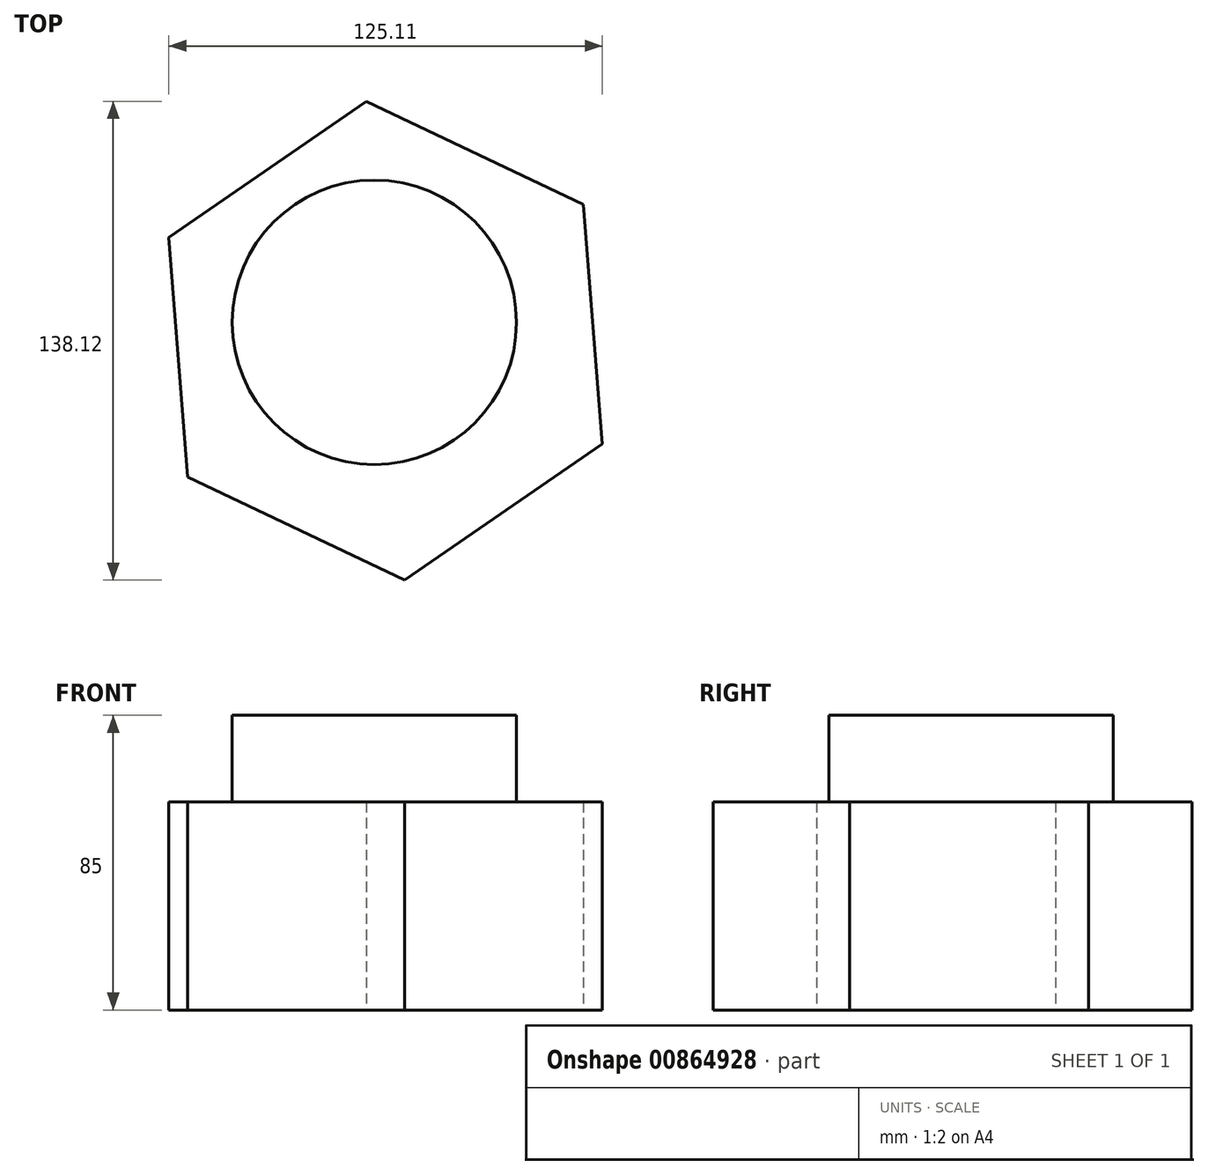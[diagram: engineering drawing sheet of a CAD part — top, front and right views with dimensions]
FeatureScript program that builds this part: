
annotation { "Feature Type Name" : "Feature", "Feature Type Description" : "" }
export const myFeature = defineFeature(function(context is Context, id is Id, definition is map)
    precondition{}
    {
        {
            var Q0;
            Q0=qCreatedBy(makeId("Top.planeOp"),FACE);
            var sketch = newSketch(context, id + "F0", { "sketchPlane" : qUnion([Q0])});
            skCircle(sketch, "E0.cCircle", {"center": v(116.54, 148.1) * mm, "radius": 60 * mm, "construction": true});
            skLineSegment(sketch, "E0.0", {"start": v(53.99, 177.88) * mm, "end": v(111.05, 217.17) * mm});
            skLineSegment(sketch, "E0.1", {"start": v(111.05, 217.17) * mm, "end": v(173.6, 187.4) * mm});
            skLineSegment(sketch, "E0.2", {"start": v(173.6, 187.4) * mm, "end": v(179.1, 118.33) * mm});
            skLineSegment(sketch, "E0.3", {"start": v(179.1, 118.33) * mm, "end": v(122.04, 79.05) * mm});
            skLineSegment(sketch, "E0.4", {"start": v(122.04, 79.05) * mm, "end": v(59.48, 108.82) * mm});
            skLineSegment(sketch, "E0.5", {"start": v(59.48, 108.82) * mm, "end": v(53.99, 177.88) * mm});
            skPoint(sketch, "E0.0.midPoint", {"position": v(82.52, 197.53) * mm});
            skSolve(sketch);
        }
        {
            var Q0;
            Q0=makeQuery(id+"F0.imprint","IMPRINT",FACE,{"disambiguationData":[TD([[makeQuery(id+"F0.imprint","IMPRINT",EDGE,{"derivedFrom":sQuery(id+"F0.wireOp",EDGE,"E0.0")}),-1.0]])]});
            extrude(context, id + "F1", {"entities" : qUnion([Q0]), "depth" : 60 * mm, "offsetDistance" : 25 * mm});
        }
        {
            var Q0;
            Q0=makeQuery(id+"F1.opExtrude","CAP_FACE",FACE,{"disambiguationData":[OSD([sQuery(id+"F0.wireOp",EDGE,"E0.0"),sQuery(id+"F0.wireOp",EDGE,"E0.1"),sQuery(id+"F0.wireOp",EDGE,"E0.2"),sQuery(id+"F0.wireOp",EDGE,"E0.3"),sQuery(id+"F0.wireOp",EDGE,"E0.4"),sQuery(id+"F0.wireOp",EDGE,"E0.5")])],"isStart":false});
            var sketch = newSketch(context, id + "F2", { "sketchPlane" : qUnion([Q0])});
            skCircle(sketch, "E1", {"center": v(113.3, 153.41) * mm, "radius": 41 * mm});
            skSolve(sketch);
        }
        {
            var Q0;
            Q0=makeQuery(id+"F2.imprint","IMPRINT",FACE,{"disambiguationData":[TD([[makeQuery(id+"F2.imprint","IMPRINT",EDGE,{"derivedFrom":sQuery(id+"F2.wireOp",EDGE,"E1")}),1.0]])]});
            extrude(context, id + "F3", {"entities" : qUnion([Q0]), "depth" : 25 * mm, "offsetDistance" : 25 * mm});
        }
    });
